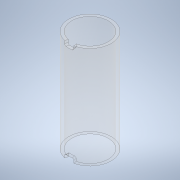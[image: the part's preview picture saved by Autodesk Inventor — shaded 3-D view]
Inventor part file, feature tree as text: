
AUTODESK INVENTOR PART (.ipt)
format: ipt  version: 2022 (Build 260153000, 153)  size: 140,800 bytes
history: native  units: in
note: dims shown in document units (in); Inventor stores cm internally (conversion verified against a paired STEP export)
features: sketch x2, extrude x1, revolve x1, fillet x1
ambient origin geometry x8: Origin, YZ Plane, XZ Plane, XY Plane, X Axis, Y Axis, Z Axis, Center Point
bodies: Body1 (feature_tree)
feature tree (5):
  extrude  "Extrusion3"  Depth=1.9528in
  revolve  "Revolution2"  [1 undecoded]
  fillet  "Fillet3"  Radius=0.1575in
  sketch  "Sketch5"  dims[d26=2.2677in d27=1.9528in]
  sketch  "Sketch6"  dims[d28=5.4488in d29=0.0in d31=0.2205in d32=0.1575in d33=0.2205in d34=0.1575in d35=0.086in d36=0.086in d37=0.0787in]
note: 1 required parameter value undecoded (feature->parameter linkage not recoverable at this tier; creation-order binding heuristic only, values carry confidence <= 0.55)
